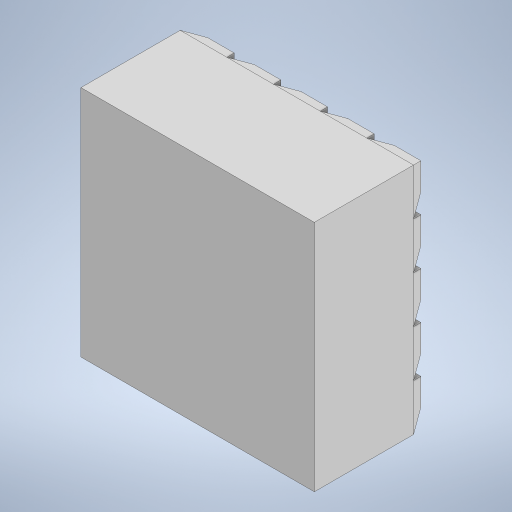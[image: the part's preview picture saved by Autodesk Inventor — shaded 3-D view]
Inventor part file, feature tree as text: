
AUTODESK INVENTOR PART (.ipt)
format: ipt  version: 2023 (Build 270158000, 158)  size: 292,864 bytes
history: native  units: in
note: dims shown in document units (in); Inventor stores cm internally (conversion verified against a paired STEP export)
features: chamfer x4, extrude x2, sketch x2, plane x2, pattern_linear x1, other x1, pattern_circular x1
ambient origin geometry x8: Origin, YZ Plane, XZ Plane, XY Plane, X Axis, Y Axis, Z Axis, Center Point
bodies: Solid1 (feature_tree)
feature tree (13):
  extrude  "Extrusion1"  Depth=1.5748in
  extrude  "Extrusion2"  Depth=0.7874in
  pattern_linear  "Rectangular Pattern1"  Spacing1=0.315in  [1 undecoded]
  other  "Work Axis1"
  pattern_circular  "Circular Pattern1"  Angle=30.0deg  [1 undecoded]
  chamfer  "Chamfer1"  Angle=30.0deg  [1 undecoded]
  chamfer  "Chamfer2"  [1 undecoded]
  chamfer  "Chamfer3"  Distance=1.5748in
  chamfer  "Chamfer4"  Distance=0.7874in Angle=90.0deg
  sketch  "Sketch1"  dims[d0=1.5748in d1=1.5748in]
  sketch  "Sketch2"  dims[d2=0.7874in d3=0.0in d4=0.1181in d5=0.315in d6=30.0deg d7=30.0deg d8=0.0in d9=0.0in d10=1.5748in d12=0.315in d13=0.7874in d14=90.0deg d16=0.1181in d17=0.0787in d18=30.0deg d19=0.1181in d20=0.0787in d21=30.0deg d22=0.1181in d23=0.0787in d24=30.0deg d25=0.1181in d26=0.0787in d27=30.0deg]
  plane  "Work Plane1"
  plane  "Work Plane2"
note: 4 required parameter values undecoded (feature->parameter linkage not recoverable at this tier; creation-order binding heuristic only, values carry confidence <= 0.55)
